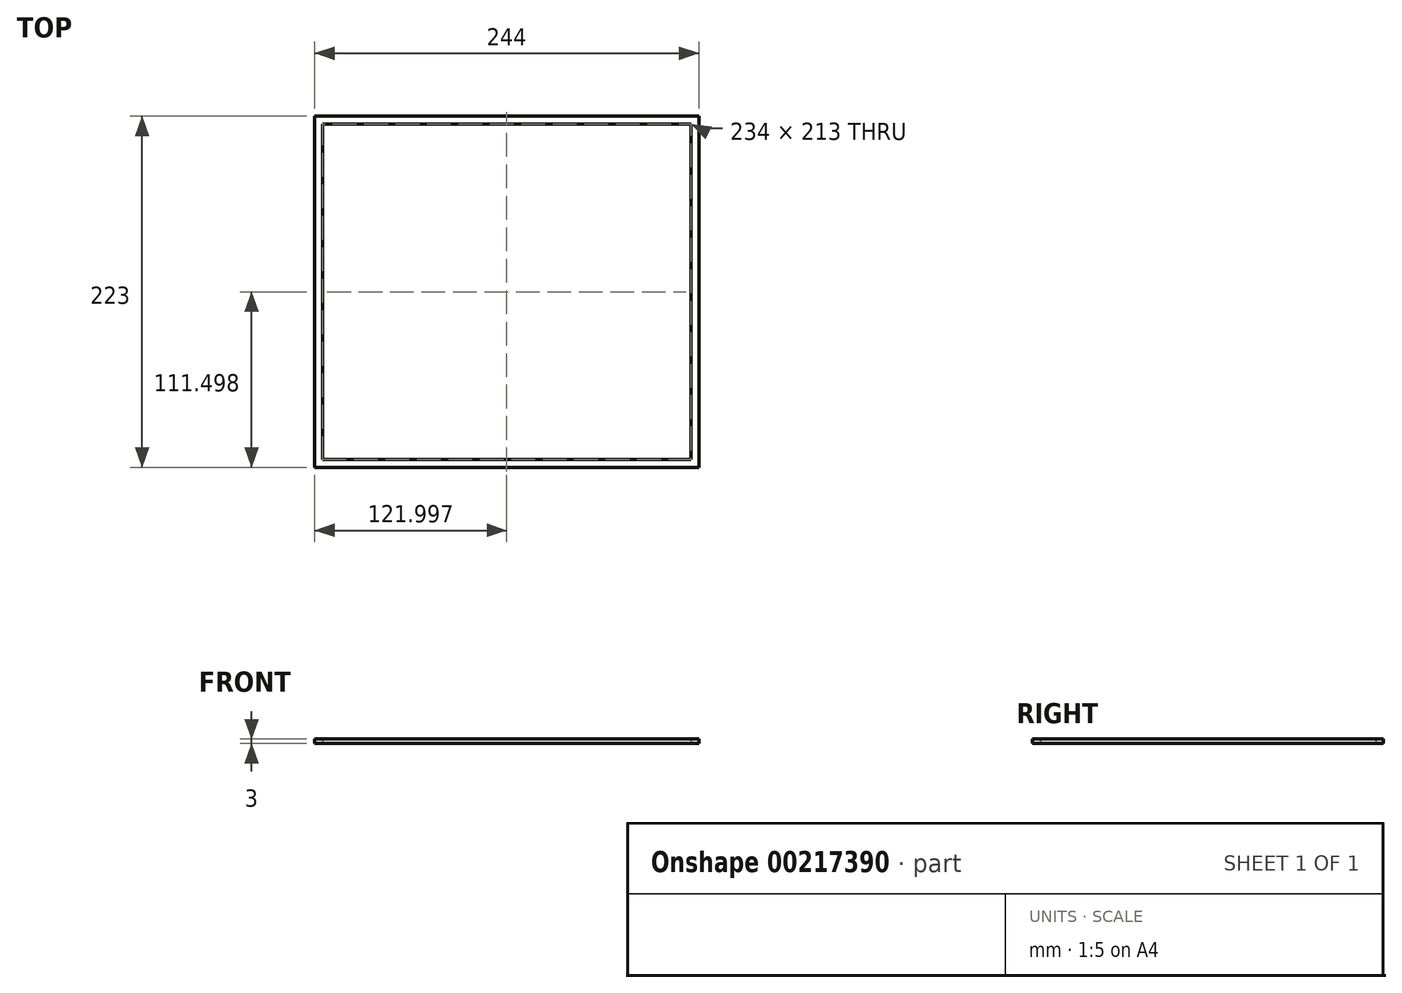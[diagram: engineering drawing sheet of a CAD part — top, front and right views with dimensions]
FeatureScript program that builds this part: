
annotation { "Feature Type Name" : "Feature", "Feature Type Description" : "" }
export const myFeature = defineFeature(function(context is Context, id is Id, definition is map)
    precondition{}
    {
        {
            var Q0;
            Q0=qCreatedBy(makeId("Top.planeOp"),FACE);
            var sketch = newSketch(context, id + "F0", { "sketchPlane" : qUnion([Q0])});
            skLineSegment(sketch, "E0.bottom", {"start": v(-130, -123) * mm, "end": v(114, -123) * mm});
            skLineSegment(sketch, "E0.top", {"start": v(-130, 100) * mm, "end": v(114, 100) * mm});
            skLineSegment(sketch, "E0.left", {"start": v(-130, -123) * mm, "end": v(-130, 100) * mm});
            skLineSegment(sketch, "E0.right", {"start": v(114, -123) * mm, "end": v(114, 100) * mm});
            skLineSegment(sketch, "E1.0", {"start": v(-125, -118) * mm, "end": v(-125, 95) * mm});
            skLineSegment(sketch, "E1.1", {"start": v(-125, -118) * mm, "end": v(109, -118) * mm});
            skLineSegment(sketch, "E1.2", {"start": v(109, -118) * mm, "end": v(109, 95) * mm});
            skLineSegment(sketch, "E1.3", {"start": v(-125, 95) * mm, "end": v(109, 95) * mm});
            skSolve(sketch);
        }
        {
            var Q0;
            Q0=makeQuery(id+"F0.imprint","IMPRINT",FACE,{"disambiguationData":[TD([[makeQuery(id+"F0.imprint","IMPRINT",EDGE,{"derivedFrom":sQuery(id+"F0.wireOp",EDGE,"E0.bottom")}),1.0]])]});
            extrude(context, id + "F1", {"entities" : qUnion([Q0]), "depth" : 3 * mm});
        }
    });
